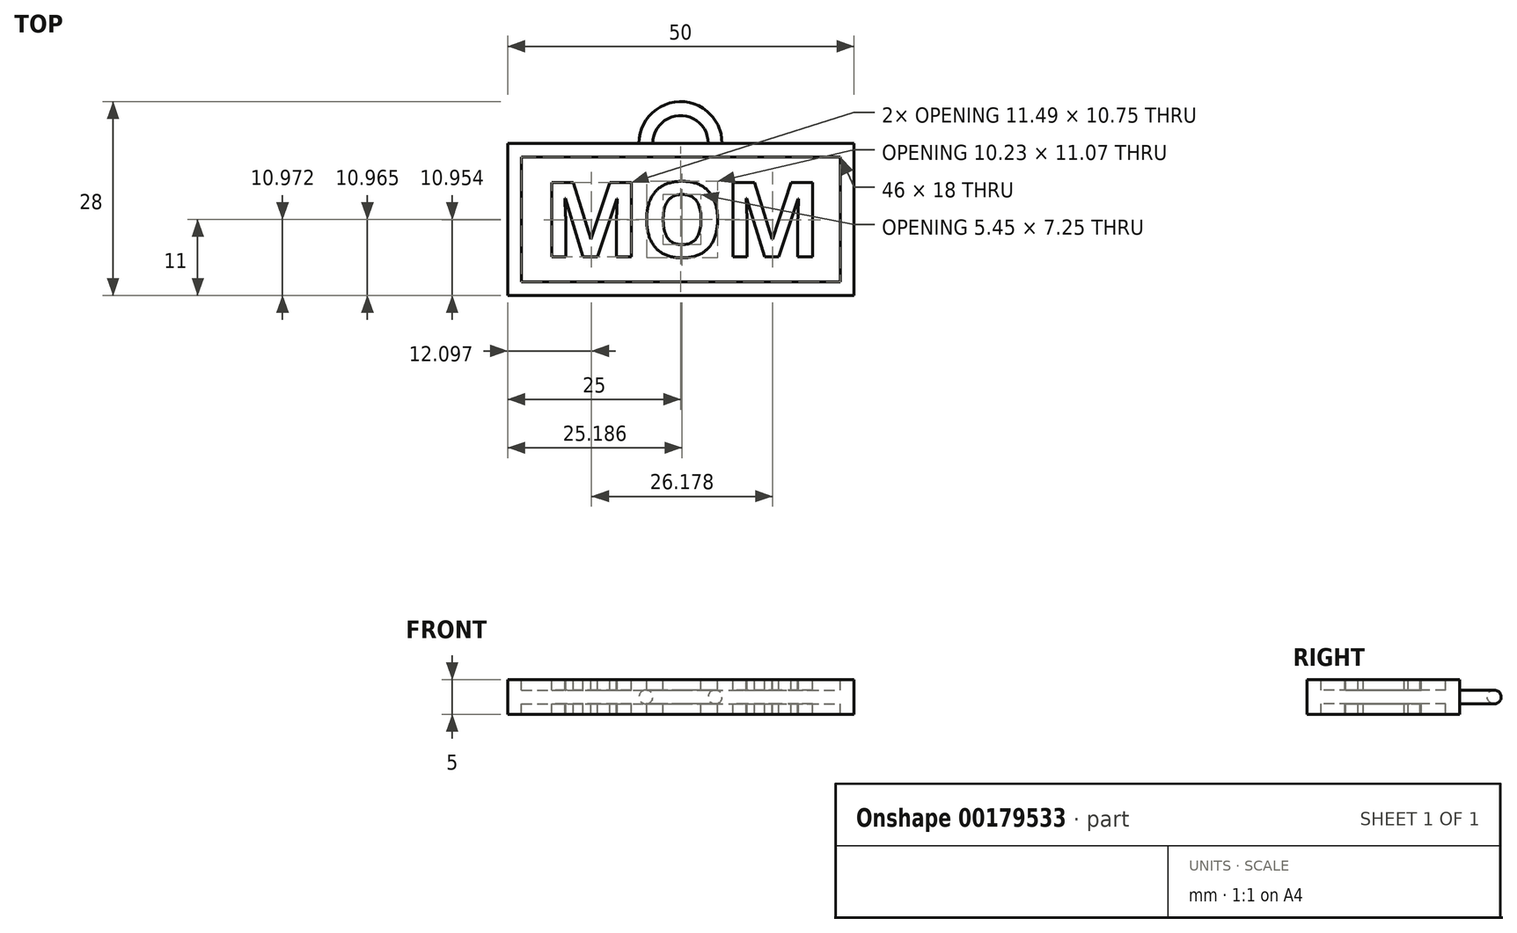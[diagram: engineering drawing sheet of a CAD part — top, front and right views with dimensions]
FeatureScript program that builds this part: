
annotation { "Feature Type Name" : "Feature", "Feature Type Description" : "" }
export const myFeature = defineFeature(function(context is Context, id is Id, definition is map)
    precondition{}
    {
        {
            var Q0;
            Q0=qCreatedBy(makeId("Top.planeOp"),FACE);
            var sketch = newSketch(context, id + "F0", { "sketchPlane" : qUnion([Q0])});
            skLineSegment(sketch, "E0.bottom", {"start": v(25, -11) * mm, "end": v(-25, -11) * mm});
            skLineSegment(sketch, "E0.left", {"start": v(25, -11) * mm, "end": v(25, 11) * mm});
            skText(sketch, "E1", { "text": "MOM", "fontName": "OpenSans-Bold.ttf"});
            skLineSegment(sketch, "E2.top", {"start": v(25, 11) * mm, "end": v(5.96, 11) * mm});
            skLineSegment(sketch, "E2.right", {"start": v(-25, -11) * mm, "end": v(-25, 11) * mm});
            skPoint(sketch, "E2.middle", {"position": v(0, 0) * mm});
            skLineSegment(sketch, "E3.bottom", {"start": v(-23, 9) * mm, "end": v(23, 9) * mm});
            skLineSegment(sketch, "E3.top", {"start": v(-23, -9) * mm, "end": v(23, -9) * mm});
            skLineSegment(sketch, "E3.left", {"start": v(-23, 9) * mm, "end": v(-23, -9) * mm});
            skLineSegment(sketch, "E3.right", {"start": v(23, 9) * mm, "end": v(23, -9) * mm});
            skArc(sketch, "E4", {"start": v(5.96, 11) * mm, "mid": v(-0.04, 17) * mm, "end": v(-6.04, 11) * mm});
            skLineSegment(sketch, "E5.trimOffspring", {"start": v(-6.04, 11) * mm, "end": v(-25, 11) * mm});
            skArc(sketch, "E6", {"start": v(-4.04, 11) * mm, "mid": v(-0.04, 15) * mm, "end": v(3.96, 11) * mm});
            skLineSegment(sketch, "E7", {"start": v(-4.04, 11) * mm, "end": v(3.96, 11) * mm});
            skLineSegment(sketch, "E8", {"start": v(-6.04, 11) * mm, "end": v(-4.04, 11) * mm});
            skLineSegment(sketch, "E9", {"start": v(3.96, 11) * mm, "end": v(5.96, 11) * mm});
            const initialGuessF0  = {"E1": [-0.02, -0.00542, 1, 0, 0.01084]};
            skSetInitialGuess(sketch, initialGuessF0);
            skSolve(sketch);
        }
        {
            var Q0;
            Q0=makeQuery(id+"F0.imprint","IMPRINT",FACE,{"disambiguationData":[TD([[makeQuery(id+"F0.imprint","IMPRINT",EDGE,{"derivedFrom":sQuery(id+"F0.wireOp",EDGE,"E1.sketch_text.stroke-0")}),1.0]])]});
            var Q1;
            Q1=makeQuery(id+"F0.imprint","IMPRINT",FACE,{"disambiguationData":[TD([[makeQuery(id+"F0.imprint","IMPRINT",EDGE,{"derivedFrom":sQuery(id+"F0.wireOp",EDGE,"E1.sketch_text.stroke-19")}),-1.0]])]});
            var Q2;
            Q2=makeQuery(id+"F0.imprint","IMPRINT",FACE,{"disambiguationData":[TD([[makeQuery(id+"F0.imprint","IMPRINT",EDGE,{"derivedFrom":sQuery(id+"F0.wireOp",EDGE,"E1.sketch_text.stroke-27")}),1.0]])]});
            var Q3;
            Q3=makeQuery(id+"F0.imprint","IMPRINT",FACE,{"disambiguationData":[TD([[makeQuery(id+"F0.imprint","IMPRINT",EDGE,{"derivedFrom":sQuery(id+"F0.wireOp",EDGE,"E1.sketch_text.stroke-0")}),-1.0]])]});
            var Q4;
            Q4=makeQuery(id+"F0.imprint","IMPRINT",FACE,{"disambiguationData":[TD([[makeQuery(id+"F0.imprint","IMPRINT",EDGE,{"derivedFrom":sQuery(id+"F0.wireOp",EDGE,"E1.sketch_text.stroke-33")}),-1.0]])]});
            var Q5;
            Q5=makeQuery(id+"F0.imprint","IMPRINT",FACE,{"disambiguationData":[TD([[makeQuery(id+"F0.imprint","IMPRINT",EDGE,{"derivedFrom":sQuery(id+"F0.wireOp",EDGE,"E0.bottom")}),-1.0]])]});
            extrude(context, id + "F1", {"entities" : qUnion([Q0, Q1, Q2, Q3, Q4, Q5]), "endBound" : BoundingType.SYMMETRIC, "depth" : 2 * mm});
        }
        {
            var Q0;
            Q0=makeQuery(id+"F0.imprint","IMPRINT",FACE,{"disambiguationData":[TD([[makeQuery(id+"F0.imprint","IMPRINT",EDGE,{"derivedFrom":sQuery(id+"F0.wireOp",EDGE,"E1.sketch_text.stroke-0")}),-1.0]])]});
            var Q1;
            Q1=makeQuery(id+"F0.imprint","IMPRINT",FACE,{"disambiguationData":[TD([[makeQuery(id+"F0.imprint","IMPRINT",EDGE,{"derivedFrom":sQuery(id+"F0.wireOp",EDGE,"E1.sketch_text.stroke-19")}),-1.0]])]});
            var Q2;
            Q2=makeQuery(id+"F0.imprint","IMPRINT",FACE,{"disambiguationData":[TD([[makeQuery(id+"F0.imprint","IMPRINT",EDGE,{"derivedFrom":sQuery(id+"F0.wireOp",EDGE,"E1.sketch_text.stroke-33")}),-1.0]])]});
            var Q3;
            Q3=makeQuery(id+"F0.imprint","IMPRINT",FACE,{"disambiguationData":[TD([[makeQuery(id+"F0.imprint","IMPRINT",EDGE,{"derivedFrom":sQuery(id+"F0.wireOp",EDGE,"E0.bottom")}),-1.0]])]});
            extrude(context, id + "F2", {"entities" : qUnion([Q0, Q1, Q2, Q3]), "operationType" : NewBodyOperationType.ADD, "endBound" : BoundingType.SYMMETRIC, "oppositeDirection" : true, "depth" : 5 * mm});
        }
        {
            var Q0;
            Q0=makeQuery(id+"F0.imprint","IMPRINT",FACE,{"disambiguationData":[TD([[makeQuery(id+"F0.imprint","IMPRINT",EDGE,{"derivedFrom":sQuery(id+"F0.wireOp",EDGE,"E4")}),1.0]])]});
            extrude(context, id + "F3", {"entities" : qUnion([Q0]), "operationType" : NewBodyOperationType.ADD, "endBound" : BoundingType.SYMMETRIC, "depth" : 2 * mm});
        }
        {
            var Q0;
            Q0=makeQuery(id+"F3.opExtrude","CAP_EDGE",EDGE,{"disambiguationData":[OSD([sQuery(id+"F0.wireOp",EDGE,"E4")])],"isStart":false});
            var Q1;
            Q1=makeQuery(id+"F3.opExtrude","CAP_EDGE",EDGE,{"disambiguationData":[OSD([sQuery(id+"F0.wireOp",EDGE,"E6")])],"isStart":false});
            var Q2;
            Q2=makeQuery(id+"F3.opExtrude","CAP_EDGE",EDGE,{"disambiguationData":[OSD([sQuery(id+"F0.wireOp",EDGE,"E6")])],"isStart":true});
            var Q3;
            Q3=makeQuery(id+"F3.opExtrude","CAP_EDGE",EDGE,{"disambiguationData":[OSD([sQuery(id+"F0.wireOp",EDGE,"E4")])],"isStart":true});
            fillet(context, id + "F4", {"entities" : qUnion([Q0, Q1, Q2, Q3]), "radius" : 1 * mm, "tangentPropagation" : true, "allowEdgeOverflow" : false});
        }
    });
